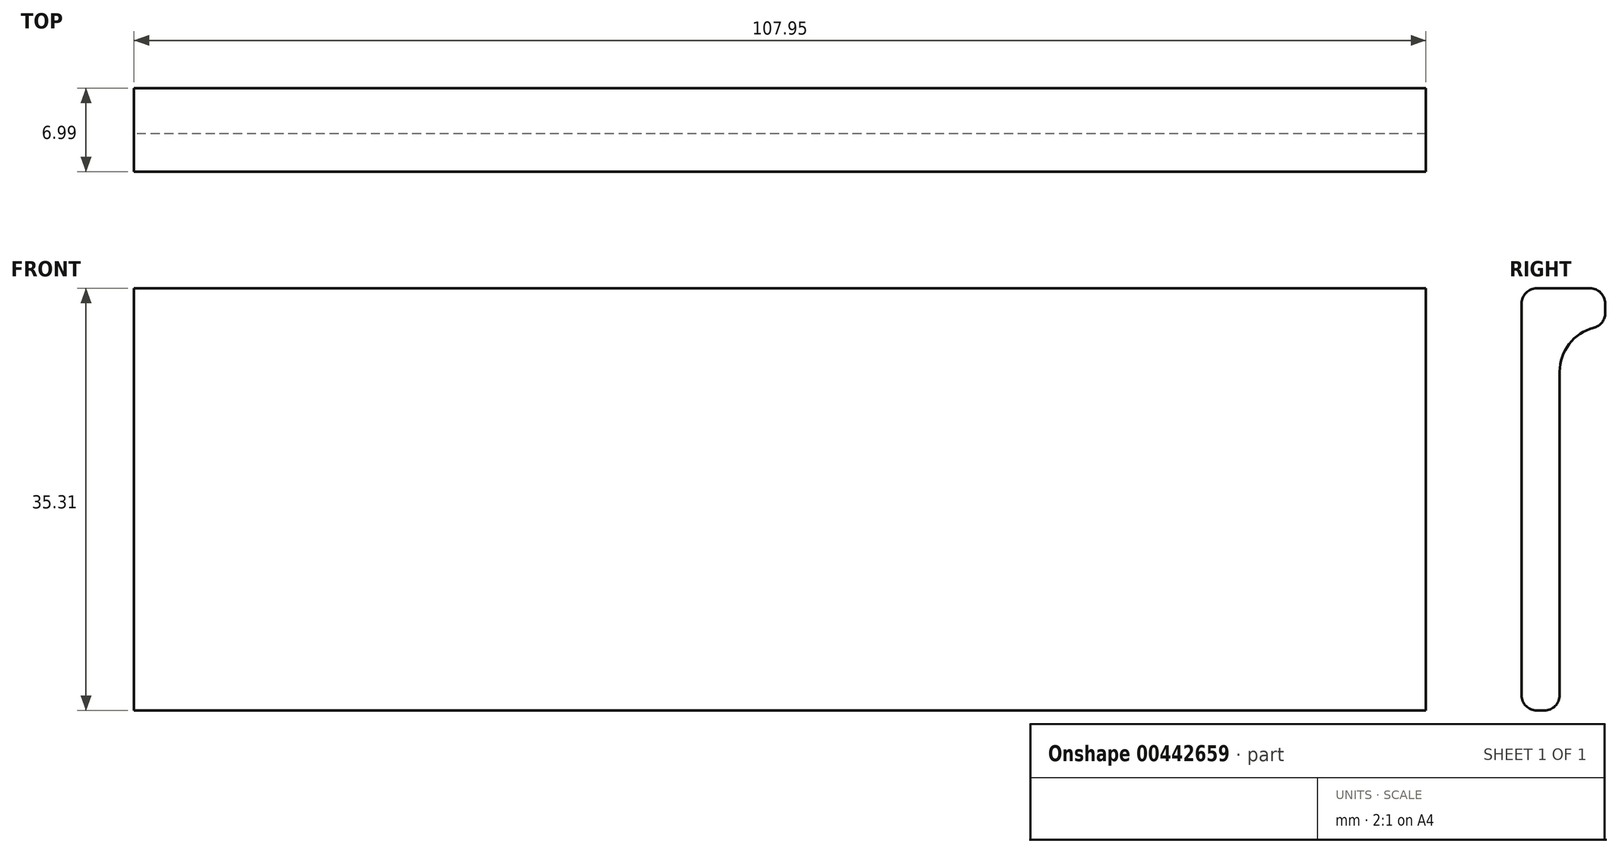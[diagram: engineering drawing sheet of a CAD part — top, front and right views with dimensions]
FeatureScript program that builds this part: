
annotation { "Feature Type Name" : "Feature", "Feature Type Description" : "" }
export const myFeature = defineFeature(function(context is Context, id is Id, definition is map)
    precondition{}
    {
        {
            var Q0;
            Q0=qCreatedBy(makeId("Right.planeOp"),FACE);
            var sketch = newSketch(context, id + "F0", { "sketchPlane" : qUnion([Q0])});
            skLineSegment(sketch, "E0", {"start": v(0, 1.27) * mm, "end": v(0, 28.96) * mm});
            skLineSegment(sketch, "E1", {"start": v(1.27, 0) * mm, "end": v(1.9, 0) * mm});
            skLineSegment(sketch, "E2", {"start": v(6.99, 34.04) * mm, "end": v(6.99, 33.24) * mm});
            skLineSegment(sketch, "E3", {"start": v(0, 28.96) * mm, "end": v(0, 34.04) * mm});
            skPoint(sketch, "E4.orphan", {"position": v(8.34, 32.13) * mm});
            skPoint(sketch, "E5.orphan", {"position": v(3.05, 28.96) * mm});
            skLineSegment(sketch, "E6", {"start": v(3.18, 1.27) * mm, "end": v(3.18, 28.32) * mm});
            skPoint(sketch, "E7.end.orphan", {"position": v(2.36, 32.13) * mm});
            skLineSegment(sketch, "E8", {"start": v(6.99, 32.13) * mm, "end": v(6.99, 32.13) * mm});
            skLineSegment(sketch, "E9", {"start": v(1.27, 35.3) * mm, "end": v(5.72, 35.3) * mm});
            skPoint(sketch, "E10.visualSharp", {"position": v(3.18, 32.13) * mm});
            skArc(sketch, "E10.filletArc", {"start": v(6.03, 32.01) * mm, "mid": v(3.97, 30.65) * mm, "end": v(3.18, 28.32) * mm});
            skPoint(sketch, "E11.visualSharp", {"position": v(6.99, 35.3) * mm});
            skArc(sketch, "E11.filletArc", {"start": v(6.99, 34.04) * mm, "mid": v(6.61, 34.93) * mm, "end": v(5.72, 35.3) * mm});
            skPoint(sketch, "E12.visualSharp", {"position": v(0, 35.3) * mm});
            skArc(sketch, "E12.filletArc", {"start": v(1.27, 35.3) * mm, "mid": v(0.37, 34.93) * mm, "end": v(0, 34.04) * mm});
            skPoint(sketch, "E13.visualSharp", {"position": v(3.18, 0) * mm});
            skArc(sketch, "E13.filletArc", {"start": v(1.9, 0) * mm, "mid": v(2.8, 0.37) * mm, "end": v(3.17, 1.27) * mm});
            skPoint(sketch, "E14.visualSharp", {"position": v(0, 0) * mm});
            skArc(sketch, "E14.filletArc", {"start": v(0, 1.27) * mm, "mid": v(0.37, 0.37) * mm, "end": v(1.27, 0) * mm});
            skPoint(sketch, "E15.visualSharp", {"position": v(6.99, 32.13) * mm});
            skArc(sketch, "E15.filletArc", {"start": v(6.03, 32.01) * mm, "mid": v(6.72, 32.46) * mm, "end": v(6.99, 33.24) * mm});
            skSolve(sketch);
        }
        {
            var Q0;
            Q0=makeQuery(id+"F0.imprint","IMPRINT",FACE,{"disambiguationData":[TD([[makeQuery(id+"F0.imprint","IMPRINT",EDGE,{"derivedFrom":sQuery(id+"F0.wireOp",EDGE,"E0")}),-1.0]])]});
            extrude(context, id + "F1", {"entities" : qUnion([Q0]), "depth" : 107.95 * mm});
        }
    });
